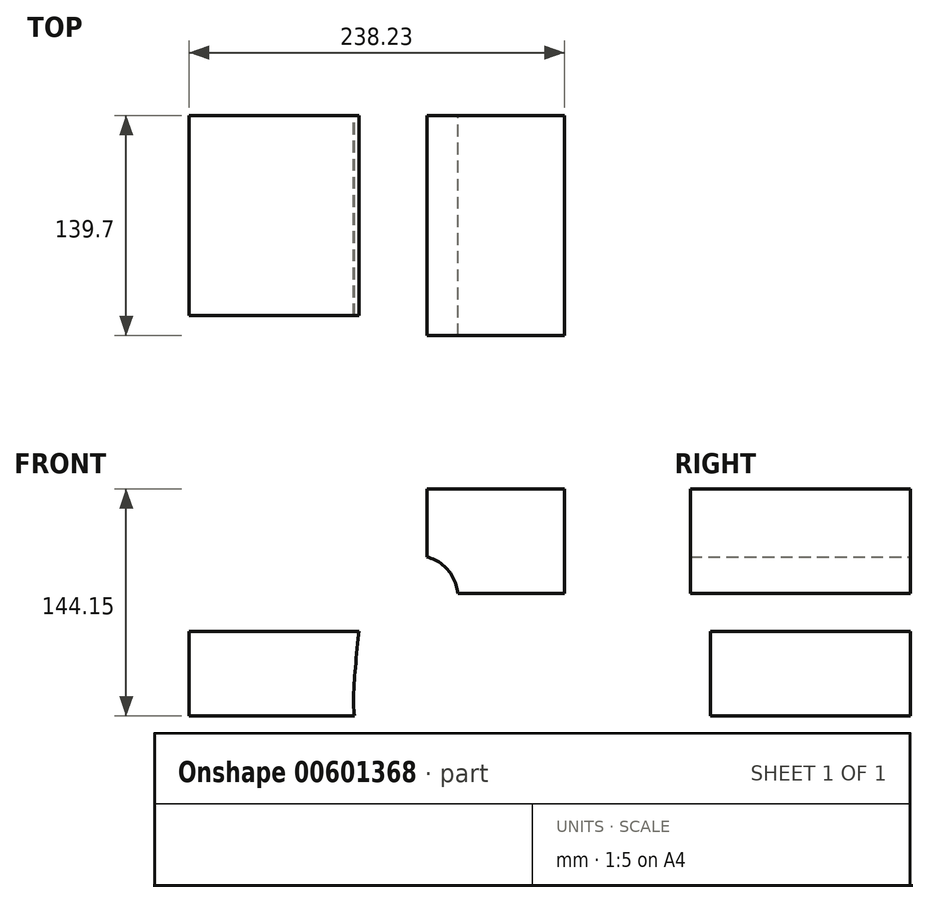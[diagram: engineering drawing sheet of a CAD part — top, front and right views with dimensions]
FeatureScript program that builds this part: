
annotation { "Feature Type Name" : "Feature", "Feature Type Description" : "" }
export const myFeature = defineFeature(function(context is Context, id is Id, definition is map)
    precondition{}
    {
        {
            var Q0;
            Q0=qCreatedBy(makeId("Front.planeOp"),FACE);
            var sketch = newSketch(context, id + "F0", { "sketchPlane" : qUnion([Q0])});
            skLineSegment(sketch, "E0.bottom", {"start": v(-63.5, 26.9) * mm, "end": v(63.5, 26.9) * mm});
            skLineSegment(sketch, "E0.top", {"start": v(-63.5, -26.9) * mm, "end": v(63.5, -26.9) * mm});
            skLineSegment(sketch, "E0.left", {"start": v(-63.5, 26.9) * mm, "end": v(-63.5, -26.9) * mm});
            skLineSegment(sketch, "E0.right", {"start": v(63.5, 26.9) * mm, "end": v(63.5, -26.9) * mm});
            skPoint(sketch, "E0.middle", {"position": v(0, 0) * mm});
            skLineSegment(sketch, "E1.bottom", {"start": v(174.73, 51) * mm, "end": v(87.57, 51) * mm});
            skLineSegment(sketch, "E1.top", {"start": v(174.73, 117.24) * mm, "end": v(87.57, 117.24) * mm});
            skLineSegment(sketch, "E1.left", {"start": v(174.73, 51) * mm, "end": v(174.73, 117.24) * mm});
            skLineSegment(sketch, "E1.right", {"start": v(87.57, 51) * mm, "end": v(87.57, 117.24) * mm});
            skPoint(sketch, "E1.middle", {"position": v(131.15, 84.12) * mm});
            skLineSegment(sketch, "E2", {"start": v(63.5, 26.9) * mm, "end": v(63.5, 51) * mm});
            skFitSpline(sketch, "E3", {"points": [v(63.5, 51) * mm, v(87.57, 51) * mm, v(63.5, -26.9) * mm, v(63.5, 26.9) * mm], "startDerivative": vector(138.53, 53.59) * mm, "endDerivative": vector(26.8, 254.26) * mm});
            skFitSpline(sketch, "E4.0", {"points": [v(56.63, 68.76) * mm, v(58.07, 69.32) * mm, v(61.12, 70.5) * mm, v(65.29, 71.99) * mm, v(68.9, 73.07) * mm, v(71.79, 73.8) * mm, v(74.91, 74.41) * mm, v(78.37, 74.8) * mm, v(81.62, 74.84) * mm, v(84.5, 74.57) * mm, v(86.78, 74.17) * mm, v(89.19, 73.53) * mm, v(91.68, 72.6) * mm, v(94.19, 71.35) * mm, v(96.64, 69.74) * mm, v(98.92, 67.82) * mm, v(100.96, 65.64) * mm, v(102.7, 63.28) * mm, v(104.1, 60.82) * mm, v(105.2, 58.35) * mm, v(106.03, 55.9) * mm, v(106.6, 53.6) * mm, v(107.1, 50.69) * mm, v(107.4, 47.29) * mm, v(107.41, 43.39) * mm, v(107.18, 39.56) * mm, v(106.75, 35.73) * mm, v(106.16, 31.87) * mm, v(105.19, 26.66) * mm, v(103.65, 20) * mm, v(101.4, 11.88) * mm, v(98.84, 3.75) * mm, v(96.05, -4.2) * mm, v(93.61, -10.56) * mm, v(91.63, -15.38) * mm, v(90.12, -18.86) * mm, v(88.62, -22.17) * mm, v(87.1, -25.3) * mm, v(85.59, -28.27) * mm, v(84.04, -31.07) * mm, v(82.7, -33.28) * mm, v(81.53, -35.03) * mm, v(80.59, -36.35) * mm, v(79.54, -37.7) * mm, v(78.51, -38.88) * mm, v(77.55, -39.88) * mm, v(76.73, -40.67) * mm, v(75.78, -41.5) * mm, v(74.65, -42.37) * mm, v(73.33, -43.27) * mm, v(71.77, -44.17) * mm, v(69.9, -45.02) * mm, v(67.71, -45.77) * mm, v(65.17, -46.3) * mm, v(62.32, -46.52) * mm, v(59.28, -46.3) * mm, v(56.25, -45.6) * mm, v(53.44, -44.46) * mm, v(50.98, -43.02) * mm, v(48.94, -41.43) * mm, v(47.31, -39.8) * mm, v(46.03, -38.23) * mm, v(44.7, -36.27) * mm, v(43.57, -34.1) * mm, v(42.72, -31.88) * mm, v(42.15, -29.97) * mm, v(41.76, -28.25) * mm, v(41.4, -26.14) * mm, v(41.12, -23.7) * mm, v(40.94, -20.85) * mm, v(40.88, -17.97) * mm, v(40.9, -15) * mm, v(41, -11.9) * mm, v(41.14, -8.68) * mm, v(41.34, -5.33) * mm, v(41.67, -0.7) * mm, v(42.18, 5.4) * mm, v(42.9, 13.05) * mm, v(43.72, 20.94) * mm, v(44.28, 26.26) * mm, v(44.55, 28.9) * mm]});
            skLineSegment(sketch, "E5", {"start": v(56.63, 68.76) * mm, "end": v(44.55, 28.9) * mm});
            skSolve(sketch);
        }
        {
            var Q0;
            {var subQ0=sQuery(id+"F0.wireOp",EDGE,"E0.left");Q0=makeQuery(id+"F0.imprint","IMPRINT",FACE,{"disambiguationData":[TD([[makeQuery(id+"F0.imprint","IMPRINT",EDGE,{"derivedFrom":subQ0}),1.0]])]});}
            var Q1;
            {var subQ1=sQuery(id+"F0.wireOp",EDGE,"E1.top");Q1=makeQuery(id+"F0.imprint","IMPRINT",FACE,{"disambiguationData":[TD([[makeQuery(id+"F0.imprint","IMPRINT",EDGE,{"derivedFrom":subQ1}),1.0]])]});}
            extrude(context, id + "F1", {"entities" : qUnion([Q0, Q1]), "endBound" : BoundingType.SYMMETRIC, "depth" : 127 * mm, "offsetDistance" : 25.4 * mm});
        }
        {
            var Q0;
            Q0=makeQuery(id+"F1.opExtrude","CAP_FACE",FACE,{"disambiguationData":[OSD([sQuery(id+"F0.wireOp",EDGE,"E1.bottom"),sQuery(id+"F0.wireOp",EDGE,"E1.top"),sQuery(id+"F0.wireOp",EDGE,"E1.left"),sQuery(id+"F0.wireOp",EDGE,"E1.right"),sQuery(id+"F0.wireOp",EDGE,"E4.0")])],"isStart":false});
            extrude(context, id + "F2", {"entities" : qUnion([Q0]), "operationType" : NewBodyOperationType.ADD, "endBound" : BoundingType.SYMMETRIC, "oppositeDirection" : true, "depth" : 25.4 * mm, "offsetDistance" : 25.4 * mm});
        }
    });
